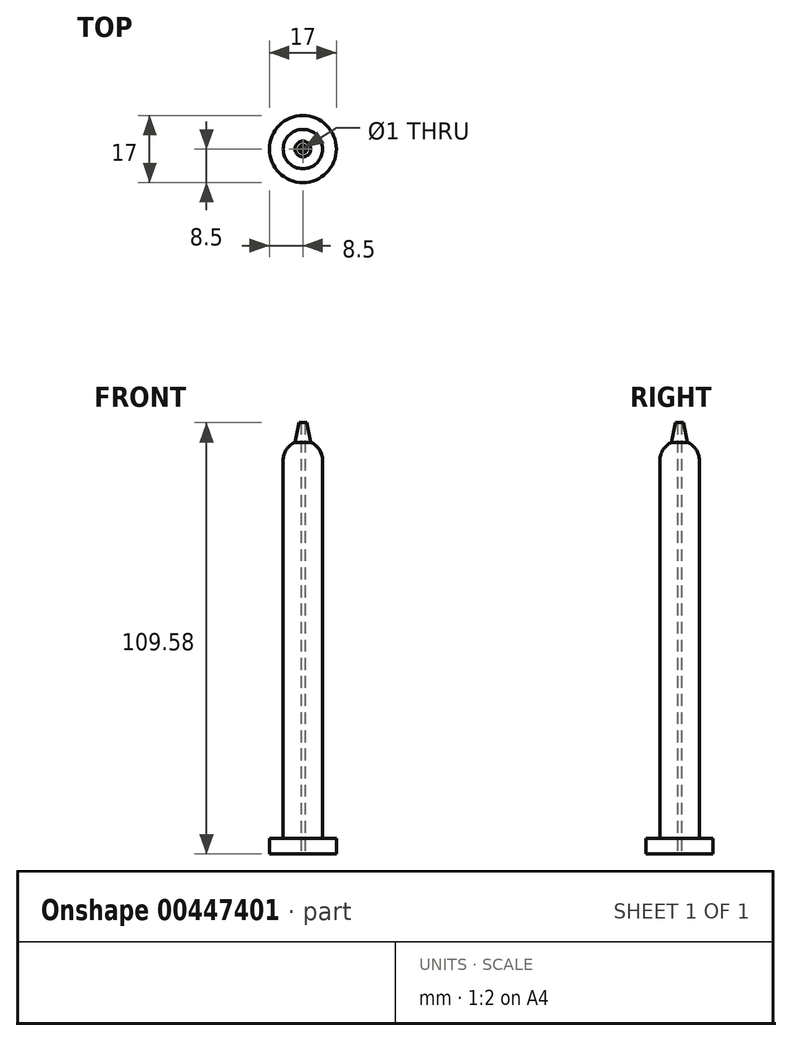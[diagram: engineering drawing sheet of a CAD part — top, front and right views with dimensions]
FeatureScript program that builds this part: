
annotation { "Feature Type Name" : "Feature", "Feature Type Description" : "" }
export const myFeature = defineFeature(function(context is Context, id is Id, definition is map)
    precondition{}
    {
        {
            var Q0;
            Q0=qCreatedBy(makeId("Top.planeOp"),FACE);
            var sketch = newSketch(context, id + "F0", { "sketchPlane" : qUnion([Q0])});
            skCircle(sketch, "E0", {"center": v(0, 0) * mm, "radius": 8.5 * mm});
            skSolve(sketch);
        }
        {
            var Q0;
            Q0=qSketchRegion(id+"F0",true);
            extrude(context, id + "F1", {"entities" : qUnion([Q0]), "depth" : 4 * mm});
        }
        {
            var Q0;
            Q0=qCreatedBy(makeId("Top.planeOp"),FACE);
            var sketch = newSketch(context, id + "F2", { "sketchPlane" : qUnion([Q0])});
            skCircle(sketch, "E1", {"center": v(0, 0) * mm, "radius": 5 * mm});
            skSolve(sketch);
        }
        {
            var Q0;
            Q0=qSketchRegion(id+"F2",true);
            extrude(context, id + "F3", {"entities" : qUnion([Q0]), "operationType" : NewBodyOperationType.ADD, "depth" : 100 * mm});
        }
        {
            var Q0;
            Q0=qCreatedBy(makeId("Right.planeOp"),FACE);
            var sketch = newSketch(context, id + "F4", { "sketchPlane" : qUnion([Q0])});
            skLineSegment(sketch, "E2", {"start": v(0, 100) * mm, "end": v(5, 100) * mm});
            skArc(sketch, "E3", {"start": v(5, 100) * mm, "mid": v(3.54, 103.54) * mm, "end": v(0, 105) * mm});
            skLineSegment(sketch, "E4", {"start": v(0, 109.58) * mm, "end": v(1, 109.58) * mm});
            skLineSegment(sketch, "E5", {"start": v(1, 109.58) * mm, "end": v(2, 104.58) * mm});
            skLineSegment(sketch, "E6", {"start": v(2, 104.58) * mm, "end": v(0, 104.58) * mm});
            skLineSegment(sketch, "E7", {"start": v(0, 109.58) * mm, "end": v(0, 100) * mm});
            skSolve(sketch);
        }
        {
            var Q0;
            {var subQ0=sQuery(id+"F4.wireOp",EDGE,"E2");Q0=makeQuery(id+"F4.imprint","IMPRINT",FACE,{"disambiguationData":[TD([[makeQuery(id+"F4.imprint","IMPRINT",EDGE,{"derivedFrom":subQ0}),1.0]])]});}
            var Q1;
            {var subQ4=sQuery(id+"F4.wireOp",EDGE,"E4");Q1=makeQuery(id+"F4.imprint","IMPRINT",FACE,{"disambiguationData":[TD([[makeQuery(id+"F4.imprint","IMPRINT",EDGE,{"derivedFrom":subQ4}),-1.0]])]});}
            var Q2;
            {var subQ3=sQuery(id+"F4.wireOp",EDGE,"E6");Q2=makeQuery(id+"F4.imprint","IMPRINT",FACE,{"disambiguationData":[TD([[makeQuery(id+"F4.imprint","IMPRINT",EDGE,{"derivedFrom":subQ3}),-1.0]])]});}
            var Q3;
            Q3=sQuery(id+"F4.wireOp",EDGE,"E7");
            revolve(context, id + "F5", {"operationType" : NewBodyOperationType.ADD, "entities" : qUnion([Q0, Q1, Q2]), "axis" : qUnion([Q3]), "revolveType" : RevolveType.FULL});
        }
        {
            var Q0;
            Q0=makeQuery(id+"F1.opExtrude","CAP_FACE",FACE,{"disambiguationData":[OSD([sQuery(id+"F0.wireOp",EDGE,"E0")])],"isStart":true});
            var sketch = newSketch(context, id + "F6", { "sketchPlane" : qUnion([Q0])});
            skCircle(sketch, "E8", {"center": v(0, 0) * mm, "radius": 0.5 * mm});
            skSolve(sketch);
        }
        {
            var Q0;
            Q0 = qSketchRegion(id + "F6", true);
            extrude(context, id + "F7", {"entities" : qUnion([Q0]), "operationType" : NewBodyOperationType.REMOVE, "oppositeDirection" : true, "depth" : 118.6 * mm});
        }
    });
